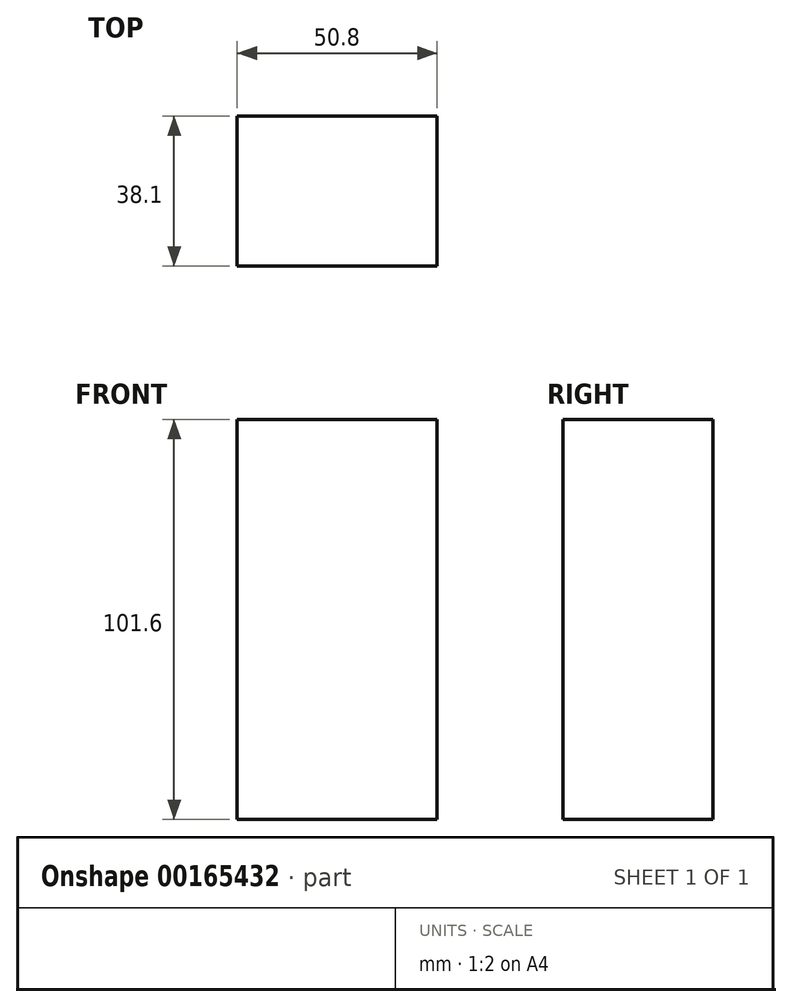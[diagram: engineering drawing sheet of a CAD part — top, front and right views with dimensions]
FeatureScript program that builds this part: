
annotation { "Feature Type Name" : "Feature", "Feature Type Description" : "" }
export const myFeature = defineFeature(function(context is Context, id is Id, definition is map)
    precondition{}
    {
        {
            var Q0;
            Q0=qCreatedBy(makeId("Top.planeOp"),FACE);
            var sketch = newSketch(context, id + "F0", { "sketchPlane" : qUnion([Q0])});
            skLineSegment(sketch, "E0.bottom", {"start": v(-26.94, 21.17) * mm, "end": v(23.86, 21.17) * mm});
            skLineSegment(sketch, "E0.top", {"start": v(-26.94, -16.93) * mm, "end": v(23.86, -16.93) * mm});
            skLineSegment(sketch, "E0.left", {"start": v(-26.94, 21.17) * mm, "end": v(-26.94, -16.93) * mm});
            skLineSegment(sketch, "E0.right", {"start": v(23.86, 21.17) * mm, "end": v(23.86, -16.93) * mm});
            skSolve(sketch);
        }
        {
            var Q0;
            Q0 = qSketchRegion(id + "F0", true);
            extrude(context, id + "F1", {"entities" : qUnion([Q0]), "depth" : 101.6 * mm});
        }
    });
